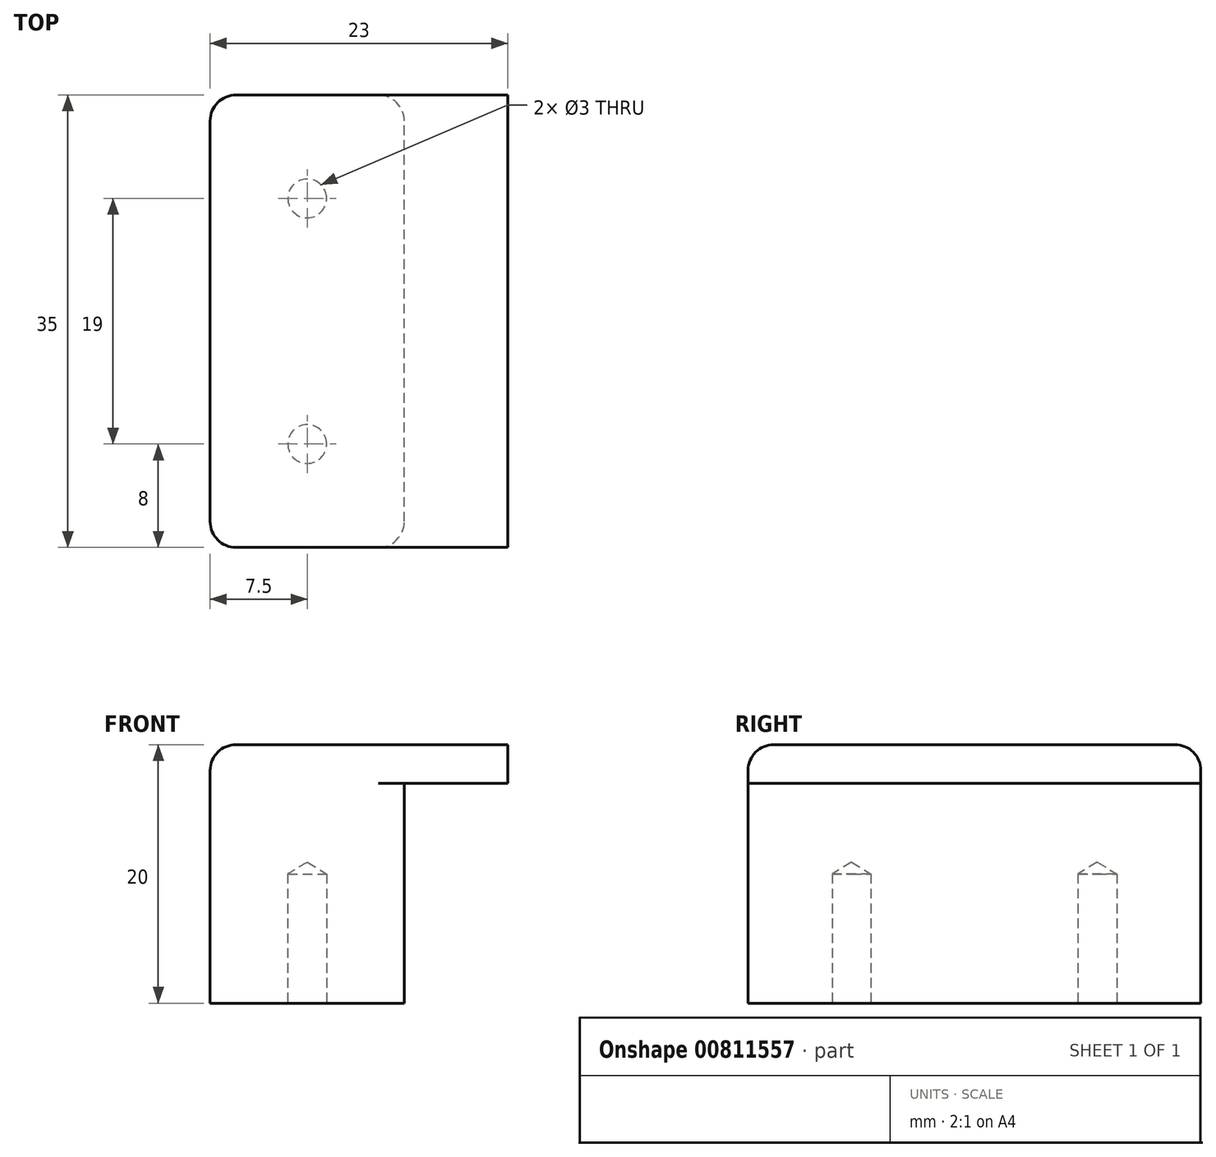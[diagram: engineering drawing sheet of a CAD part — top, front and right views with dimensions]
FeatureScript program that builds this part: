
annotation { "Feature Type Name" : "Feature", "Feature Type Description" : "" }
export const myFeature = defineFeature(function(context is Context, id is Id, definition is map)
    precondition{}
    {
        {
            var Q0;
            Q0=qCreatedBy(makeId("Top.planeOp"),FACE);
            var sketch = newSketch(context, id + "F0", { "sketchPlane" : qUnion([Q0])});
            skLineSegment(sketch, "E0.bottom", {"start": v(7.5, -17.5) * mm, "end": v(-7.5, -17.5) * mm});
            skLineSegment(sketch, "E0.top", {"start": v(7.5, 17.5) * mm, "end": v(-7.5, 17.5) * mm});
            skLineSegment(sketch, "E0.left", {"start": v(7.5, -17.5) * mm, "end": v(7.5, 17.5) * mm});
            skLineSegment(sketch, "E0.right", {"start": v(-7.5, -17.5) * mm, "end": v(-7.5, 17.5) * mm});
            skPoint(sketch, "E0.middle", {"position": v(0, 0) * mm});
            skSolve(sketch);
        }
        {
            var Q0;
            Q0 = qSketchRegion(id + "F0", true);
            extrude(context, id + "F1", {"entities" : qUnion([Q0]), "depth" : 17 * mm, "offsetDistance" : 25 * mm});
        }
        {
            var Q0;
            Q0=makeQuery(id+"F1.opExtrude","CAP_FACE",FACE,{"disambiguationData":[OSD([sQuery(id+"F0.wireOp",EDGE,"E0.bottom"),sQuery(id+"F0.wireOp",EDGE,"E0.top"),sQuery(id+"F0.wireOp",EDGE,"E0.left"),sQuery(id+"F0.wireOp",EDGE,"E0.right")])],"isStart":false});
            var sketch = newSketch(context, id + "F2", { "sketchPlane" : qUnion([Q0])});
            skLineSegment(sketch, "E1.bottom", {"start": v(-7.5, 17.5) * mm, "end": v(15.5, 17.5) * mm});
            skLineSegment(sketch, "E1.top", {"start": v(-7.5, -17.5) * mm, "end": v(15.5, -17.5) * mm});
            skLineSegment(sketch, "E1.left", {"start": v(-7.5, 17.5) * mm, "end": v(-7.5, -17.5) * mm});
            skLineSegment(sketch, "E1.right", {"start": v(15.5, 17.5) * mm, "end": v(15.5, -17.5) * mm});
            skSolve(sketch);
        }
        {
            var Q0;
            Q0 = qSketchRegion(id + "F2", true);
            extrude(context, id + "F3", {"entities" : qUnion([Q0]), "operationType" : NewBodyOperationType.ADD, "depth" : 3 * mm, "offsetDistance" : 25 * mm});
        }
        {
            var Q0;
            Q0=makeQuery(id+"F1.opExtrude","CAP_FACE",FACE,{"disambiguationData":[OSD([sQuery(id+"F0.wireOp",EDGE,"E0.bottom"),sQuery(id+"F0.wireOp",EDGE,"E0.top"),sQuery(id+"F0.wireOp",EDGE,"E0.left"),sQuery(id+"F0.wireOp",EDGE,"E0.right")])],"isStart":true});
            var sketch = newSketch(context, id + "F4", { "sketchPlane" : qUnion([Q0])});
            skPoint(sketch, "E2", {"position": v(0, 9.5) * mm});
            skPoint(sketch, "E3", {"position": v(0, -9.5) * mm});
            skSolve(sketch);
        }
        {
            var Q0;
            Q0=sQuery(id+"F4.wireOp",VERTEX,"E2");
            var Q1;
            Q1=sQuery(id+"F4.wireOp",VERTEX,"E3");
            var Q2;
            Q2=makeQuery(id+"F1.opExtrude","SWEPT_BODY",BODY,{"disambiguationData":[OSD([sQuery(id+"F0.wireOp",EDGE,"E0.bottom"),sQuery(id+"F0.wireOp",EDGE,"E0.top"),sQuery(id+"F0.wireOp",EDGE,"E0.left"),sQuery(id+"F0.wireOp",EDGE,"E0.right")])]});
            hole(context, id + "F5", {"style" : HoleStyle.SIMPLE, "endStyle" : HoleEndStyle.BLIND, "holeDiameter" : 3 * mm, "majorDiameter" : 5 * mm, "holeDepth" : 10 * mm, "isTappedThrough" : true, "tappedDepth" : 12 * mm, "tapClearance" : 3, "locations" : qUnion([Q0, Q1]), "scope" : qUnion([Q2])});
        }
        {
            var Q0;
            Q0=makeQuery(id+"F3.opExtrude","CAP_EDGE",EDGE,{"disambiguationData":[OSD([sQuery(id+"F2.wireOp",EDGE,"E1.left")])],"isStart":false});
            var Q1;
            Q1=makeQuery(id+"F3.boolean.opBoolean","MERGE",EDGE,{"derivedFrom":[makeQuery(id+"F1.opExtrude","SWEPT_EDGE",EDGE,{"disambiguationData":[OSD([sQuery(id+"F0.wireOp",EDGE,"E0.bottom"),sQuery(id+"F0.wireOp",EDGE,"E0.right")])]}),makeQuery(id+"F3.opExtrude","SWEPT_EDGE",EDGE,{"disambiguationData":[OSD([sQuery(id+"F2.wireOp",EDGE,"E1.top"),sQuery(id+"F2.wireOp",EDGE,"E1.left")])]})]});
            var Q2;
            Q2=makeQuery(id+"F3.boolean.opBoolean","MERGE",EDGE,{"derivedFrom":[makeQuery(id+"F1.opExtrude","SWEPT_EDGE",EDGE,{"disambiguationData":[OSD([sQuery(id+"F0.wireOp",EDGE,"E0.top"),sQuery(id+"F0.wireOp",EDGE,"E0.right")])]}),makeQuery(id+"F3.opExtrude","SWEPT_EDGE",EDGE,{"disambiguationData":[OSD([sQuery(id+"F2.wireOp",EDGE,"E1.bottom"),sQuery(id+"F2.wireOp",EDGE,"E1.left")])]})]});
            var Q3;
            Q3=makeQuery(id+"F3.opExtrude","CAP_EDGE",EDGE,{"disambiguationData":[OSD([sQuery(id+"F2.wireOp",EDGE,"E1.top")])],"isStart":false});
            var Q4;
            Q4=makeQuery(id+"F3.opExtrude","CAP_EDGE",EDGE,{"disambiguationData":[OSD([sQuery(id+"F2.wireOp",EDGE,"E1.bottom")])],"isStart":false});
            var Q5;
            Q5=makeQuery(id+"F1.opExtrude","CAP_EDGE",EDGE,{"disambiguationData":[OSD([sQuery(id+"F0.wireOp",EDGE,"E0.left")])],"isStart":false});
            var Q6;
            Q6=makeQuery(id+"F1.opExtrude","SWEPT_EDGE",EDGE,{"disambiguationData":[OSD([sQuery(id+"F0.wireOp",EDGE,"E0.bottom"),sQuery(id+"F0.wireOp",EDGE,"E0.left")])]});
            var Q7;
            Q7=makeQuery(id+"F1.opExtrude","SWEPT_EDGE",EDGE,{"disambiguationData":[OSD([sQuery(id+"F0.wireOp",EDGE,"E0.top"),sQuery(id+"F0.wireOp",EDGE,"E0.left")])]});
            fillet(context, id + "F6", {"entities" : qUnion([Q0, Q1, Q2, Q3, Q4, Q5, Q6, Q7]), "radius" : 2 * mm, "tangentPropagation" : true, "allowEdgeOverflow" : false});
        }
    });
